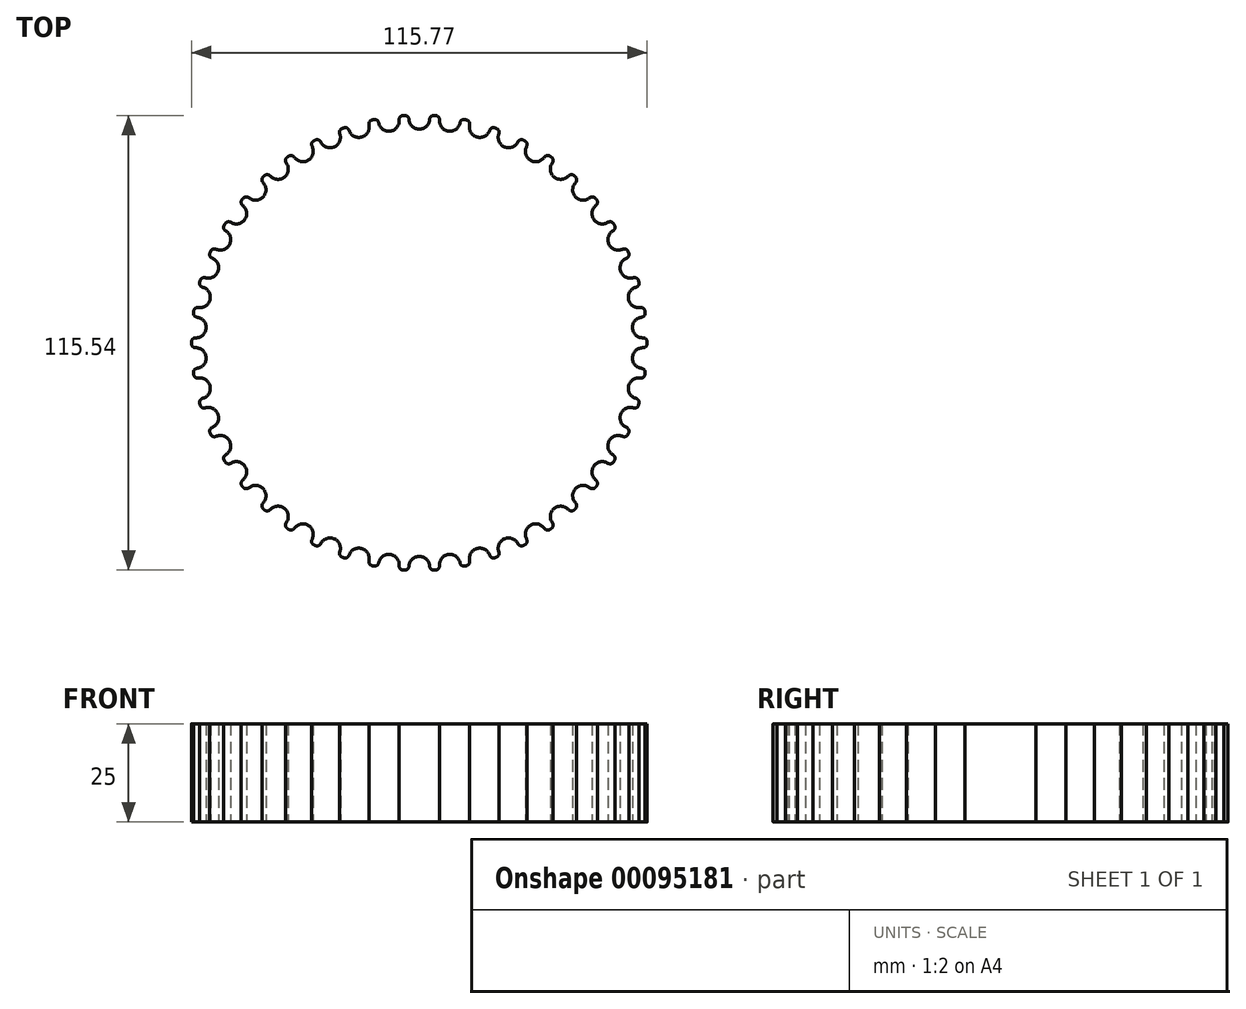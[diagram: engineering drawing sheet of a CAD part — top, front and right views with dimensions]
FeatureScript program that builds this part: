
annotation { "Feature Type Name" : "Feature", "Feature Type Description" : "" }
export const myFeature = defineFeature(function(context is Context, id is Id, definition is map)
    precondition{}
    {
        {
            var Q0;
            Q0=qCreatedBy(makeId("Top.planeOp"),FACE);
            var sketch = newSketch(context, id + "F0", { "sketchPlane" : qUnion([Q0])});
            skArc(sketch, "E0", {"start": v(-3.73, 57.76) * mm, "mid": v(-3.95, 57.75) * mm, "end": v(-4.17, 57.73) * mm});
            skCircle(sketch, "E1", {"center": v(0, 0) * mm, "radius": 54.28 * mm, "construction": true});
            skLineSegment(sketch, "E2", {"start": v(0, 0) * mm, "end": v(0, 57.88) * mm, "construction": true});
            skArc(sketch, "E3", {"start": v(-2.6, 56.59) * mm, "mid": v(0, 54.28) * mm, "end": v(2.6, 56.59) * mm});
            skArc(sketch, "E4", {"start": v(-2.64, 56.87) * mm, "mid": v(-3, 57.53) * mm, "end": v(-3.73, 57.76) * mm});
            skArc(sketch, "E5", {"start": v(3.73, 57.76) * mm, "mid": v(3, 57.53) * mm, "end": v(2.64, 56.87) * mm});
            skLineSegment(sketch, "E6", {"start": v(-2.64, 56.87) * mm, "end": v(-2.6, 56.59) * mm});
            skLineSegment(sketch, "E7", {"start": v(2.6, 56.59) * mm, "end": v(2.64, 56.87) * mm});
            skArc(sketch, "E8.1.0", {"start": v(-10.36, 55.98) * mm, "mid": v(-10.81, 56.59) * mm, "end": v(-11.56, 56.72) * mm});
            skLineSegment(sketch, "E8.1.1", {"start": v(-10.36, 55.98) * mm, "end": v(-10.3, 55.7) * mm});
            skArc(sketch, "E8.1.2", {"start": v(-10.3, 55.7) * mm, "mid": v(-7.4, 53.78) * mm, "end": v(-5.12, 56.42) * mm});
            skLineSegment(sketch, "E8.1.3", {"start": v(-5.12, 56.42) * mm, "end": v(-5.12, 56.7) * mm});
            skArc(sketch, "E8.1.4", {"start": v(-4.17, 57.73) * mm, "mid": v(-4.86, 57.4) * mm, "end": v(-5.12, 56.7) * mm});
            skArc(sketch, "E8.2.0", {"start": v(-17.89, 54.05) * mm, "mid": v(-18.42, 54.59) * mm, "end": v(-19.17, 54.62) * mm});
            skLineSegment(sketch, "E8.2.1", {"start": v(-17.89, 54.05) * mm, "end": v(-17.78, 53.79) * mm});
            skArc(sketch, "E8.2.2", {"start": v(-17.78, 53.79) * mm, "mid": v(-14.64, 52.27) * mm, "end": v(-12.76, 55.2) * mm});
            skLineSegment(sketch, "E8.2.3", {"start": v(-12.76, 55.2) * mm, "end": v(-12.8, 55.47) * mm});
            skArc(sketch, "E8.2.4", {"start": v(-12, 56.63) * mm, "mid": v(-12.63, 56.2) * mm, "end": v(-12.8, 55.47) * mm});
            skArc(sketch, "E8.3.0", {"start": v(-25.08, 51.1) * mm, "mid": v(-25.68, 51.57) * mm, "end": v(-26.43, 51.5) * mm});
            skLineSegment(sketch, "E8.3.1", {"start": v(-25.08, 51.1) * mm, "end": v(-24.94, 50.87) * mm});
            skArc(sketch, "E8.3.2", {"start": v(-24.94, 50.87) * mm, "mid": v(-21.63, 49.79) * mm, "end": v(-20.15, 52.94) * mm});
            skLineSegment(sketch, "E8.3.3", {"start": v(-20.15, 52.94) * mm, "end": v(-20.23, 53.21) * mm});
            skArc(sketch, "E8.3.4", {"start": v(-19.6, 54.47) * mm, "mid": v(-20.16, 53.97) * mm, "end": v(-20.23, 53.21) * mm});
            skArc(sketch, "E8.4.0", {"start": v(-31.8, 47.22) * mm, "mid": v(-32.46, 47.6) * mm, "end": v(-33.2, 47.42) * mm});
            skLineSegment(sketch, "E8.4.1", {"start": v(-31.8, 47.22) * mm, "end": v(-31.63, 47) * mm});
            skArc(sketch, "E8.4.2", {"start": v(-31.63, 47) * mm, "mid": v(-28.2, 46.38) * mm, "end": v(-27.17, 49.7) * mm});
            skLineSegment(sketch, "E8.4.3", {"start": v(-27.17, 49.7) * mm, "end": v(-27.29, 49.96) * mm});
            skArc(sketch, "E8.4.4", {"start": v(-26.83, 51.3) * mm, "mid": v(-27.32, 50.72) * mm, "end": v(-27.29, 49.96) * mm});
            skArc(sketch, "E8.5.0", {"start": v(-37.94, 42.44) * mm, "mid": v(-38.64, 42.73) * mm, "end": v(-39.34, 42.46) * mm});
            skLineSegment(sketch, "E8.5.1", {"start": v(-37.94, 42.44) * mm, "end": v(-37.74, 42.25) * mm});
            skArc(sketch, "E8.5.2", {"start": v(-37.74, 42.25) * mm, "mid": v(-34.26, 42.1) * mm, "end": v(-33.69, 45.54) * mm});
            skLineSegment(sketch, "E8.5.3", {"start": v(-33.69, 45.54) * mm, "end": v(-33.84, 45.78) * mm});
            skArc(sketch, "E8.5.4", {"start": v(-33.56, 47.16) * mm, "mid": v(-33.98, 46.53) * mm, "end": v(-33.84, 45.78) * mm});
            skArc(sketch, "E8.6.0", {"start": v(-43.37, 36.88) * mm, "mid": v(-44.1, 37.07) * mm, "end": v(-44.76, 36.7) * mm});
            skLineSegment(sketch, "E8.6.1", {"start": v(-43.37, 36.88) * mm, "end": v(-43.14, 36.72) * mm});
            skArc(sketch, "E8.6.2", {"start": v(-43.14, 36.72) * mm, "mid": v(-39.67, 37.05) * mm, "end": v(-39.58, 40.53) * mm});
            skLineSegment(sketch, "E8.6.3", {"start": v(-39.58, 40.53) * mm, "end": v(-39.76, 40.75) * mm});
            skArc(sketch, "E8.6.4", {"start": v(-39.67, 42.15) * mm, "mid": v(-40, 41.47) * mm, "end": v(-39.76, 40.75) * mm});
            skArc(sketch, "E8.7.0", {"start": v(-47.98, 30.63) * mm, "mid": v(-48.74, 30.72) * mm, "end": v(-49.34, 30.27) * mm});
            skLineSegment(sketch, "E8.7.1", {"start": v(-47.98, 30.63) * mm, "end": v(-47.74, 30.5) * mm});
            skArc(sketch, "E8.7.2", {"start": v(-47.74, 30.5) * mm, "mid": v(-44.35, 31.3) * mm, "end": v(-44.73, 34.77) * mm});
            skLineSegment(sketch, "E8.7.3", {"start": v(-44.73, 34.77) * mm, "end": v(-44.93, 34.95) * mm});
            skArc(sketch, "E8.7.4", {"start": v(-45.04, 36.36) * mm, "mid": v(-45.27, 35.63) * mm, "end": v(-44.93, 34.95) * mm});
            skArc(sketch, "E8.8.0", {"start": v(-51.7, 23.82) * mm, "mid": v(-52.46, 23.8) * mm, "end": v(-53, 23.27) * mm});
            skLineSegment(sketch, "E8.8.1", {"start": v(-51.7, 23.82) * mm, "end": v(-51.45, 23.72) * mm});
            skArc(sketch, "E8.8.2", {"start": v(-51.45, 23.72) * mm, "mid": v(-48.2, 24.97) * mm, "end": v(-49.04, 28.35) * mm});
            skLineSegment(sketch, "E8.8.3", {"start": v(-49.04, 28.35) * mm, "end": v(-49.28, 28.51) * mm});
            skArc(sketch, "E8.8.4", {"start": v(-49.57, 29.88) * mm, "mid": v(-49.7, 29.14) * mm, "end": v(-49.28, 28.51) * mm});
            skArc(sketch, "E8.9.0", {"start": v(-54.47, 16.55) * mm, "mid": v(-55.22, 16.43) * mm, "end": v(-55.68, 15.83) * mm});
            skLineSegment(sketch, "E8.9.1", {"start": v(-54.47, 16.55) * mm, "end": v(-54.2, 16.5) * mm});
            skArc(sketch, "E8.9.2", {"start": v(-54.2, 16.5) * mm, "mid": v(-51.15, 18.18) * mm, "end": v(-52.45, 21.4) * mm});
            skLineSegment(sketch, "E8.9.3", {"start": v(-52.45, 21.4) * mm, "end": v(-52.7, 21.53) * mm});
            skArc(sketch, "E8.9.4", {"start": v(-53.18, 22.86) * mm, "mid": v(-53.2, 22.1) * mm, "end": v(-52.7, 21.53) * mm});
            skArc(sketch, "E8.10.0", {"start": v(-56.22, 8.98) * mm, "mid": v(-56.94, 8.76) * mm, "end": v(-57.31, 8.1) * mm});
            skLineSegment(sketch, "E8.10.1", {"start": v(-56.22, 8.98) * mm, "end": v(-55.94, 8.96) * mm});
            skArc(sketch, "E8.10.2", {"start": v(-55.94, 8.96) * mm, "mid": v(-53.15, 11.04) * mm, "end": v(-54.88, 14.07) * mm});
            skLineSegment(sketch, "E8.10.3", {"start": v(-54.88, 14.07) * mm, "end": v(-55.14, 14.16) * mm});
            skArc(sketch, "E8.10.4", {"start": v(-55.8, 15.4) * mm, "mid": v(-55.72, 14.65) * mm, "end": v(-55.14, 14.16) * mm});
            skArc(sketch, "E8.11.0", {"start": v(-56.92, 1.24) * mm, "mid": v(-57.6, 0.93) * mm, "end": v(-57.88, 0.22) * mm});
            skLineSegment(sketch, "E8.11.1", {"start": v(-56.92, 1.24) * mm, "end": v(-56.64, 1.26) * mm});
            skArc(sketch, "E8.11.2", {"start": v(-56.64, 1.26) * mm, "mid": v(-54.15, 3.7) * mm, "end": v(-56.28, 6.47) * mm});
            skLineSegment(sketch, "E8.11.3", {"start": v(-56.28, 6.47) * mm, "end": v(-56.55, 6.52) * mm});
            skArc(sketch, "E8.11.4", {"start": v(-57.38, 7.66) * mm, "mid": v(-57.2, 6.93) * mm, "end": v(-56.55, 6.52) * mm});
            skArc(sketch, "E8.12.0", {"start": v(-56.55, -6.52) * mm, "mid": v(-57.2, -6.93) * mm, "end": v(-57.38, -7.66) * mm});
            skLineSegment(sketch, "E8.12.1", {"start": v(-56.55, -6.52) * mm, "end": v(-56.28, -6.47) * mm});
            skArc(sketch, "E8.12.2", {"start": v(-56.28, -6.47) * mm, "mid": v(-54.15, -3.7) * mm, "end": v(-56.64, -1.26) * mm});
            skLineSegment(sketch, "E8.12.3", {"start": v(-56.64, -1.26) * mm, "end": v(-56.92, -1.24) * mm});
            skArc(sketch, "E8.12.4", {"start": v(-57.88, -0.22) * mm, "mid": v(-57.6, -0.93) * mm, "end": v(-56.92, -1.24) * mm});
            skArc(sketch, "E8.13.0", {"start": v(-55.14, -14.16) * mm, "mid": v(-55.72, -14.65) * mm, "end": v(-55.8, -15.4) * mm});
            skLineSegment(sketch, "E8.13.1", {"start": v(-55.14, -14.16) * mm, "end": v(-54.88, -14.07) * mm});
            skArc(sketch, "E8.13.2", {"start": v(-54.88, -14.07) * mm, "mid": v(-53.15, -11.04) * mm, "end": v(-55.94, -8.96) * mm});
            skLineSegment(sketch, "E8.13.3", {"start": v(-55.94, -8.96) * mm, "end": v(-56.22, -8.98) * mm});
            skArc(sketch, "E8.13.4", {"start": v(-57.31, -8.1) * mm, "mid": v(-56.94, -8.76) * mm, "end": v(-56.22, -8.98) * mm});
            skArc(sketch, "E8.14.0", {"start": v(-52.7, -21.53) * mm, "mid": v(-53.2, -22.1) * mm, "end": v(-53.18, -22.86) * mm});
            skLineSegment(sketch, "E8.14.1", {"start": v(-52.7, -21.53) * mm, "end": v(-52.45, -21.4) * mm});
            skArc(sketch, "E8.14.2", {"start": v(-52.45, -21.4) * mm, "mid": v(-51.15, -18.18) * mm, "end": v(-54.2, -16.5) * mm});
            skLineSegment(sketch, "E8.14.3", {"start": v(-54.2, -16.5) * mm, "end": v(-54.47, -16.55) * mm});
            skArc(sketch, "E8.14.4", {"start": v(-55.68, -15.83) * mm, "mid": v(-55.22, -16.43) * mm, "end": v(-54.47, -16.55) * mm});
            skArc(sketch, "E8.15.0", {"start": v(-49.28, -28.51) * mm, "mid": v(-49.7, -29.14) * mm, "end": v(-49.57, -29.88) * mm});
            skLineSegment(sketch, "E8.15.1", {"start": v(-49.28, -28.51) * mm, "end": v(-49.04, -28.35) * mm});
            skArc(sketch, "E8.15.2", {"start": v(-49.04, -28.35) * mm, "mid": v(-48.2, -24.97) * mm, "end": v(-51.45, -23.72) * mm});
            skLineSegment(sketch, "E8.15.3", {"start": v(-51.45, -23.72) * mm, "end": v(-51.7, -23.82) * mm});
            skArc(sketch, "E8.15.4", {"start": v(-53, -23.27) * mm, "mid": v(-52.46, -23.8) * mm, "end": v(-51.7, -23.82) * mm});
            skArc(sketch, "E8.16.0", {"start": v(-44.93, -34.95) * mm, "mid": v(-45.27, -35.63) * mm, "end": v(-45.04, -36.36) * mm});
            skLineSegment(sketch, "E8.16.1", {"start": v(-44.93, -34.95) * mm, "end": v(-44.73, -34.77) * mm});
            skArc(sketch, "E8.16.2", {"start": v(-44.73, -34.77) * mm, "mid": v(-44.35, -31.3) * mm, "end": v(-47.74, -30.5) * mm});
            skLineSegment(sketch, "E8.16.3", {"start": v(-47.74, -30.5) * mm, "end": v(-47.98, -30.63) * mm});
            skArc(sketch, "E8.16.4", {"start": v(-49.34, -30.27) * mm, "mid": v(-48.74, -30.72) * mm, "end": v(-47.98, -30.63) * mm});
            skArc(sketch, "E8.17.0", {"start": v(-39.76, -40.75) * mm, "mid": v(-40, -41.47) * mm, "end": v(-39.67, -42.15) * mm});
            skLineSegment(sketch, "E8.17.1", {"start": v(-39.76, -40.75) * mm, "end": v(-39.58, -40.53) * mm});
            skArc(sketch, "E8.17.2", {"start": v(-39.58, -40.53) * mm, "mid": v(-39.67, -37.05) * mm, "end": v(-43.14, -36.72) * mm});
            skLineSegment(sketch, "E8.17.3", {"start": v(-43.14, -36.72) * mm, "end": v(-43.37, -36.88) * mm});
            skArc(sketch, "E8.17.4", {"start": v(-44.76, -36.7) * mm, "mid": v(-44.1, -37.07) * mm, "end": v(-43.37, -36.88) * mm});
            skArc(sketch, "E8.18.0", {"start": v(-33.84, -45.78) * mm, "mid": v(-33.98, -46.53) * mm, "end": v(-33.56, -47.16) * mm});
            skLineSegment(sketch, "E8.18.1", {"start": v(-33.84, -45.78) * mm, "end": v(-33.69, -45.54) * mm});
            skArc(sketch, "E8.18.2", {"start": v(-33.69, -45.54) * mm, "mid": v(-34.26, -42.1) * mm, "end": v(-37.74, -42.25) * mm});
            skLineSegment(sketch, "E8.18.3", {"start": v(-37.74, -42.25) * mm, "end": v(-37.94, -42.44) * mm});
            skArc(sketch, "E8.18.4", {"start": v(-39.34, -42.46) * mm, "mid": v(-38.64, -42.73) * mm, "end": v(-37.94, -42.44) * mm});
            skArc(sketch, "E8.19.0", {"start": v(-27.29, -49.96) * mm, "mid": v(-27.32, -50.72) * mm, "end": v(-26.83, -51.3) * mm});
            skLineSegment(sketch, "E8.19.1", {"start": v(-27.29, -49.96) * mm, "end": v(-27.17, -49.7) * mm});
            skArc(sketch, "E8.19.2", {"start": v(-27.17, -49.7) * mm, "mid": v(-28.2, -46.38) * mm, "end": v(-31.63, -47) * mm});
            skLineSegment(sketch, "E8.19.3", {"start": v(-31.63, -47) * mm, "end": v(-31.8, -47.22) * mm});
            skArc(sketch, "E8.19.4", {"start": v(-33.2, -47.42) * mm, "mid": v(-32.46, -47.6) * mm, "end": v(-31.8, -47.22) * mm});
            skArc(sketch, "E8.20.0", {"start": v(-20.23, -53.21) * mm, "mid": v(-20.16, -53.97) * mm, "end": v(-19.6, -54.47) * mm});
            skLineSegment(sketch, "E8.20.1", {"start": v(-20.23, -53.21) * mm, "end": v(-20.15, -52.94) * mm});
            skArc(sketch, "E8.20.2", {"start": v(-20.15, -52.94) * mm, "mid": v(-21.63, -49.79) * mm, "end": v(-24.94, -50.87) * mm});
            skLineSegment(sketch, "E8.20.3", {"start": v(-24.94, -50.87) * mm, "end": v(-25.08, -51.1) * mm});
            skArc(sketch, "E8.20.4", {"start": v(-26.43, -51.5) * mm, "mid": v(-25.68, -51.57) * mm, "end": v(-25.08, -51.1) * mm});
            skArc(sketch, "E8.21.0", {"start": v(-12.8, -55.47) * mm, "mid": v(-12.63, -56.2) * mm, "end": v(-12, -56.63) * mm});
            skLineSegment(sketch, "E8.21.1", {"start": v(-12.8, -55.47) * mm, "end": v(-12.76, -55.2) * mm});
            skArc(sketch, "E8.21.2", {"start": v(-12.76, -55.2) * mm, "mid": v(-14.64, -52.27) * mm, "end": v(-17.78, -53.79) * mm});
            skLineSegment(sketch, "E8.21.3", {"start": v(-17.78, -53.79) * mm, "end": v(-17.89, -54.05) * mm});
            skArc(sketch, "E8.21.4", {"start": v(-19.17, -54.62) * mm, "mid": v(-18.42, -54.59) * mm, "end": v(-17.89, -54.05) * mm});
            skArc(sketch, "E8.22.0", {"start": v(-5.12, -56.7) * mm, "mid": v(-4.86, -57.4) * mm, "end": v(-4.17, -57.73) * mm});
            skLineSegment(sketch, "E8.22.1", {"start": v(-5.12, -56.7) * mm, "end": v(-5.12, -56.42) * mm});
            skArc(sketch, "E8.22.2", {"start": v(-5.12, -56.42) * mm, "mid": v(-7.4, -53.78) * mm, "end": v(-10.3, -55.7) * mm});
            skLineSegment(sketch, "E8.22.3", {"start": v(-10.3, -55.7) * mm, "end": v(-10.36, -55.98) * mm});
            skArc(sketch, "E8.22.4", {"start": v(-11.56, -56.72) * mm, "mid": v(-10.81, -56.59) * mm, "end": v(-10.36, -55.98) * mm});
            skArc(sketch, "E8.23.0", {"start": v(2.64, -56.87) * mm, "mid": v(3, -57.53) * mm, "end": v(3.73, -57.76) * mm});
            skLineSegment(sketch, "E8.23.1", {"start": v(2.64, -56.87) * mm, "end": v(2.6, -56.59) * mm});
            skArc(sketch, "E8.23.2", {"start": v(2.6, -56.59) * mm, "mid": v(0, -54.28) * mm, "end": v(-2.6, -56.59) * mm});
            skLineSegment(sketch, "E8.23.3", {"start": v(-2.6, -56.59) * mm, "end": v(-2.64, -56.87) * mm});
            skArc(sketch, "E8.23.4", {"start": v(-3.73, -57.76) * mm, "mid": v(-3, -57.53) * mm, "end": v(-2.64, -56.87) * mm});
            skArc(sketch, "E8.24.0", {"start": v(10.36, -55.98) * mm, "mid": v(10.81, -56.59) * mm, "end": v(11.56, -56.72) * mm});
            skLineSegment(sketch, "E8.24.1", {"start": v(10.36, -55.98) * mm, "end": v(10.3, -55.7) * mm});
            skArc(sketch, "E8.24.2", {"start": v(10.3, -55.7) * mm, "mid": v(7.4, -53.78) * mm, "end": v(5.12, -56.42) * mm});
            skLineSegment(sketch, "E8.24.3", {"start": v(5.12, -56.42) * mm, "end": v(5.12, -56.7) * mm});
            skArc(sketch, "E8.24.4", {"start": v(4.17, -57.73) * mm, "mid": v(4.86, -57.4) * mm, "end": v(5.12, -56.7) * mm});
            skArc(sketch, "E8.25.0", {"start": v(17.89, -54.05) * mm, "mid": v(18.42, -54.59) * mm, "end": v(19.17, -54.62) * mm});
            skLineSegment(sketch, "E8.25.1", {"start": v(17.89, -54.05) * mm, "end": v(17.78, -53.79) * mm});
            skArc(sketch, "E8.25.2", {"start": v(17.78, -53.79) * mm, "mid": v(14.64, -52.27) * mm, "end": v(12.76, -55.2) * mm});
            skLineSegment(sketch, "E8.25.3", {"start": v(12.76, -55.2) * mm, "end": v(12.8, -55.47) * mm});
            skArc(sketch, "E8.25.4", {"start": v(12, -56.63) * mm, "mid": v(12.63, -56.2) * mm, "end": v(12.8, -55.47) * mm});
            skArc(sketch, "E8.26.0", {"start": v(25.08, -51.1) * mm, "mid": v(25.68, -51.57) * mm, "end": v(26.43, -51.5) * mm});
            skLineSegment(sketch, "E8.26.1", {"start": v(25.08, -51.1) * mm, "end": v(24.94, -50.87) * mm});
            skArc(sketch, "E8.26.2", {"start": v(24.94, -50.87) * mm, "mid": v(21.63, -49.79) * mm, "end": v(20.15, -52.94) * mm});
            skLineSegment(sketch, "E8.26.3", {"start": v(20.15, -52.94) * mm, "end": v(20.23, -53.21) * mm});
            skArc(sketch, "E8.26.4", {"start": v(19.6, -54.47) * mm, "mid": v(20.16, -53.97) * mm, "end": v(20.23, -53.21) * mm});
            skArc(sketch, "E8.27.0", {"start": v(31.8, -47.22) * mm, "mid": v(32.46, -47.6) * mm, "end": v(33.2, -47.42) * mm});
            skLineSegment(sketch, "E8.27.1", {"start": v(31.8, -47.22) * mm, "end": v(31.63, -47) * mm});
            skArc(sketch, "E8.27.2", {"start": v(31.63, -47) * mm, "mid": v(28.2, -46.38) * mm, "end": v(27.17, -49.7) * mm});
            skLineSegment(sketch, "E8.27.3", {"start": v(27.17, -49.7) * mm, "end": v(27.29, -49.96) * mm});
            skArc(sketch, "E8.27.4", {"start": v(26.83, -51.3) * mm, "mid": v(27.32, -50.72) * mm, "end": v(27.29, -49.96) * mm});
            skArc(sketch, "E8.28.0", {"start": v(37.94, -42.44) * mm, "mid": v(38.64, -42.73) * mm, "end": v(39.34, -42.46) * mm});
            skLineSegment(sketch, "E8.28.1", {"start": v(37.94, -42.44) * mm, "end": v(37.74, -42.25) * mm});
            skArc(sketch, "E8.28.2", {"start": v(37.74, -42.25) * mm, "mid": v(34.26, -42.1) * mm, "end": v(33.69, -45.54) * mm});
            skLineSegment(sketch, "E8.28.3", {"start": v(33.69, -45.54) * mm, "end": v(33.84, -45.78) * mm});
            skArc(sketch, "E8.28.4", {"start": v(33.56, -47.16) * mm, "mid": v(33.98, -46.53) * mm, "end": v(33.84, -45.78) * mm});
            skArc(sketch, "E8.29.0", {"start": v(43.37, -36.88) * mm, "mid": v(44.1, -37.07) * mm, "end": v(44.76, -36.7) * mm});
            skLineSegment(sketch, "E8.29.1", {"start": v(43.37, -36.88) * mm, "end": v(43.14, -36.72) * mm});
            skArc(sketch, "E8.29.2", {"start": v(43.14, -36.72) * mm, "mid": v(39.67, -37.05) * mm, "end": v(39.58, -40.53) * mm});
            skLineSegment(sketch, "E8.29.3", {"start": v(39.58, -40.53) * mm, "end": v(39.76, -40.75) * mm});
            skArc(sketch, "E8.29.4", {"start": v(39.67, -42.15) * mm, "mid": v(40, -41.47) * mm, "end": v(39.76, -40.75) * mm});
            skArc(sketch, "E8.30.0", {"start": v(47.98, -30.63) * mm, "mid": v(48.74, -30.72) * mm, "end": v(49.34, -30.27) * mm});
            skLineSegment(sketch, "E8.30.1", {"start": v(47.98, -30.63) * mm, "end": v(47.74, -30.5) * mm});
            skArc(sketch, "E8.30.2", {"start": v(47.74, -30.5) * mm, "mid": v(44.35, -31.3) * mm, "end": v(44.73, -34.77) * mm});
            skLineSegment(sketch, "E8.30.3", {"start": v(44.73, -34.77) * mm, "end": v(44.93, -34.95) * mm});
            skArc(sketch, "E8.30.4", {"start": v(45.04, -36.36) * mm, "mid": v(45.27, -35.63) * mm, "end": v(44.93, -34.95) * mm});
            skArc(sketch, "E8.31.0", {"start": v(51.7, -23.82) * mm, "mid": v(52.46, -23.8) * mm, "end": v(53, -23.27) * mm});
            skLineSegment(sketch, "E8.31.1", {"start": v(51.7, -23.82) * mm, "end": v(51.45, -23.72) * mm});
            skArc(sketch, "E8.31.2", {"start": v(51.45, -23.72) * mm, "mid": v(48.2, -24.97) * mm, "end": v(49.04, -28.35) * mm});
            skLineSegment(sketch, "E8.31.3", {"start": v(49.04, -28.35) * mm, "end": v(49.28, -28.51) * mm});
            skArc(sketch, "E8.31.4", {"start": v(49.57, -29.88) * mm, "mid": v(49.7, -29.14) * mm, "end": v(49.28, -28.51) * mm});
            skArc(sketch, "E8.32.0", {"start": v(54.47, -16.55) * mm, "mid": v(55.22, -16.43) * mm, "end": v(55.68, -15.83) * mm});
            skLineSegment(sketch, "E8.32.1", {"start": v(54.47, -16.55) * mm, "end": v(54.2, -16.5) * mm});
            skArc(sketch, "E8.32.2", {"start": v(54.2, -16.5) * mm, "mid": v(51.15, -18.18) * mm, "end": v(52.45, -21.4) * mm});
            skLineSegment(sketch, "E8.32.3", {"start": v(52.45, -21.4) * mm, "end": v(52.7, -21.53) * mm});
            skArc(sketch, "E8.32.4", {"start": v(53.18, -22.86) * mm, "mid": v(53.2, -22.1) * mm, "end": v(52.7, -21.53) * mm});
            skArc(sketch, "E8.33.0", {"start": v(56.22, -8.98) * mm, "mid": v(56.94, -8.76) * mm, "end": v(57.31, -8.1) * mm});
            skLineSegment(sketch, "E8.33.1", {"start": v(56.22, -8.98) * mm, "end": v(55.94, -8.96) * mm});
            skArc(sketch, "E8.33.2", {"start": v(55.94, -8.96) * mm, "mid": v(53.15, -11.04) * mm, "end": v(54.88, -14.07) * mm});
            skLineSegment(sketch, "E8.33.3", {"start": v(54.88, -14.07) * mm, "end": v(55.14, -14.16) * mm});
            skArc(sketch, "E8.33.4", {"start": v(55.8, -15.4) * mm, "mid": v(55.72, -14.65) * mm, "end": v(55.14, -14.16) * mm});
            skArc(sketch, "E8.34.0", {"start": v(56.92, -1.24) * mm, "mid": v(57.6, -0.93) * mm, "end": v(57.88, -0.22) * mm});
            skLineSegment(sketch, "E8.34.1", {"start": v(56.92, -1.24) * mm, "end": v(56.64, -1.26) * mm});
            skArc(sketch, "E8.34.2", {"start": v(56.64, -1.26) * mm, "mid": v(54.15, -3.7) * mm, "end": v(56.28, -6.47) * mm});
            skLineSegment(sketch, "E8.34.3", {"start": v(56.28, -6.47) * mm, "end": v(56.55, -6.52) * mm});
            skArc(sketch, "E8.34.4", {"start": v(57.38, -7.66) * mm, "mid": v(57.2, -6.93) * mm, "end": v(56.55, -6.52) * mm});
            skArc(sketch, "E8.35.0", {"start": v(56.55, 6.52) * mm, "mid": v(57.2, 6.93) * mm, "end": v(57.38, 7.66) * mm});
            skLineSegment(sketch, "E8.35.1", {"start": v(56.55, 6.52) * mm, "end": v(56.28, 6.47) * mm});
            skArc(sketch, "E8.35.2", {"start": v(56.28, 6.47) * mm, "mid": v(54.15, 3.7) * mm, "end": v(56.64, 1.26) * mm});
            skLineSegment(sketch, "E8.35.3", {"start": v(56.64, 1.26) * mm, "end": v(56.92, 1.24) * mm});
            skArc(sketch, "E8.35.4", {"start": v(57.88, 0.22) * mm, "mid": v(57.6, 0.93) * mm, "end": v(56.92, 1.24) * mm});
            skArc(sketch, "E8.36.0", {"start": v(55.14, 14.16) * mm, "mid": v(55.72, 14.65) * mm, "end": v(55.8, 15.4) * mm});
            skLineSegment(sketch, "E8.36.1", {"start": v(55.14, 14.16) * mm, "end": v(54.88, 14.07) * mm});
            skArc(sketch, "E8.36.2", {"start": v(54.88, 14.07) * mm, "mid": v(53.15, 11.04) * mm, "end": v(55.94, 8.96) * mm});
            skLineSegment(sketch, "E8.36.3", {"start": v(55.94, 8.96) * mm, "end": v(56.22, 8.98) * mm});
            skArc(sketch, "E8.36.4", {"start": v(57.31, 8.1) * mm, "mid": v(56.94, 8.76) * mm, "end": v(56.22, 8.98) * mm});
            skArc(sketch, "E8.37.0", {"start": v(52.7, 21.53) * mm, "mid": v(53.2, 22.1) * mm, "end": v(53.18, 22.86) * mm});
            skLineSegment(sketch, "E8.37.1", {"start": v(52.7, 21.53) * mm, "end": v(52.45, 21.4) * mm});
            skArc(sketch, "E8.37.2", {"start": v(52.45, 21.4) * mm, "mid": v(51.15, 18.18) * mm, "end": v(54.2, 16.5) * mm});
            skLineSegment(sketch, "E8.37.3", {"start": v(54.2, 16.5) * mm, "end": v(54.47, 16.55) * mm});
            skArc(sketch, "E8.37.4", {"start": v(55.68, 15.83) * mm, "mid": v(55.22, 16.43) * mm, "end": v(54.47, 16.55) * mm});
            skArc(sketch, "E8.38.0", {"start": v(49.28, 28.51) * mm, "mid": v(49.7, 29.14) * mm, "end": v(49.57, 29.88) * mm});
            skLineSegment(sketch, "E8.38.1", {"start": v(49.28, 28.51) * mm, "end": v(49.04, 28.35) * mm});
            skArc(sketch, "E8.38.2", {"start": v(49.04, 28.35) * mm, "mid": v(48.2, 24.97) * mm, "end": v(51.45, 23.72) * mm});
            skLineSegment(sketch, "E8.38.3", {"start": v(51.45, 23.72) * mm, "end": v(51.7, 23.82) * mm});
            skArc(sketch, "E8.38.4", {"start": v(53, 23.27) * mm, "mid": v(52.46, 23.8) * mm, "end": v(51.7, 23.82) * mm});
            skArc(sketch, "E8.39.0", {"start": v(44.93, 34.95) * mm, "mid": v(45.27, 35.63) * mm, "end": v(45.04, 36.36) * mm});
            skLineSegment(sketch, "E8.39.1", {"start": v(44.93, 34.95) * mm, "end": v(44.73, 34.77) * mm});
            skArc(sketch, "E8.39.2", {"start": v(44.73, 34.77) * mm, "mid": v(44.35, 31.3) * mm, "end": v(47.74, 30.5) * mm});
            skLineSegment(sketch, "E8.39.3", {"start": v(47.74, 30.5) * mm, "end": v(47.98, 30.63) * mm});
            skArc(sketch, "E8.39.4", {"start": v(49.34, 30.27) * mm, "mid": v(48.74, 30.72) * mm, "end": v(47.98, 30.63) * mm});
            skArc(sketch, "E8.40.0", {"start": v(39.76, 40.75) * mm, "mid": v(40, 41.47) * mm, "end": v(39.67, 42.15) * mm});
            skLineSegment(sketch, "E8.40.1", {"start": v(39.76, 40.75) * mm, "end": v(39.58, 40.53) * mm});
            skArc(sketch, "E8.40.2", {"start": v(39.58, 40.53) * mm, "mid": v(39.67, 37.05) * mm, "end": v(43.14, 36.72) * mm});
            skLineSegment(sketch, "E8.40.3", {"start": v(43.14, 36.72) * mm, "end": v(43.37, 36.88) * mm});
            skArc(sketch, "E8.40.4", {"start": v(44.76, 36.7) * mm, "mid": v(44.1, 37.07) * mm, "end": v(43.37, 36.88) * mm});
            skArc(sketch, "E8.41.0", {"start": v(33.84, 45.78) * mm, "mid": v(33.98, 46.53) * mm, "end": v(33.56, 47.16) * mm});
            skLineSegment(sketch, "E8.41.1", {"start": v(33.84, 45.78) * mm, "end": v(33.69, 45.54) * mm});
            skArc(sketch, "E8.41.2", {"start": v(33.69, 45.54) * mm, "mid": v(34.26, 42.1) * mm, "end": v(37.74, 42.25) * mm});
            skLineSegment(sketch, "E8.41.3", {"start": v(37.74, 42.25) * mm, "end": v(37.94, 42.44) * mm});
            skArc(sketch, "E8.41.4", {"start": v(39.34, 42.46) * mm, "mid": v(38.64, 42.73) * mm, "end": v(37.94, 42.44) * mm});
            skArc(sketch, "E8.42.0", {"start": v(27.29, 49.96) * mm, "mid": v(27.32, 50.72) * mm, "end": v(26.83, 51.3) * mm});
            skLineSegment(sketch, "E8.42.1", {"start": v(27.29, 49.96) * mm, "end": v(27.17, 49.7) * mm});
            skArc(sketch, "E8.42.2", {"start": v(27.17, 49.7) * mm, "mid": v(28.2, 46.38) * mm, "end": v(31.63, 47) * mm});
            skLineSegment(sketch, "E8.42.3", {"start": v(31.63, 47) * mm, "end": v(31.8, 47.22) * mm});
            skArc(sketch, "E8.42.4", {"start": v(33.2, 47.42) * mm, "mid": v(32.46, 47.6) * mm, "end": v(31.8, 47.22) * mm});
            skArc(sketch, "E8.43.0", {"start": v(20.23, 53.21) * mm, "mid": v(20.16, 53.97) * mm, "end": v(19.6, 54.47) * mm});
            skLineSegment(sketch, "E8.43.1", {"start": v(20.23, 53.21) * mm, "end": v(20.15, 52.94) * mm});
            skArc(sketch, "E8.43.2", {"start": v(20.15, 52.94) * mm, "mid": v(21.63, 49.79) * mm, "end": v(24.94, 50.87) * mm});
            skLineSegment(sketch, "E8.43.3", {"start": v(24.94, 50.87) * mm, "end": v(25.08, 51.1) * mm});
            skArc(sketch, "E8.43.4", {"start": v(26.43, 51.5) * mm, "mid": v(25.68, 51.57) * mm, "end": v(25.08, 51.1) * mm});
            skArc(sketch, "E8.44.0", {"start": v(12.8, 55.47) * mm, "mid": v(12.63, 56.2) * mm, "end": v(12, 56.63) * mm});
            skLineSegment(sketch, "E8.44.1", {"start": v(12.8, 55.47) * mm, "end": v(12.76, 55.2) * mm});
            skArc(sketch, "E8.44.2", {"start": v(12.76, 55.2) * mm, "mid": v(14.64, 52.27) * mm, "end": v(17.78, 53.79) * mm});
            skLineSegment(sketch, "E8.44.3", {"start": v(17.78, 53.79) * mm, "end": v(17.89, 54.05) * mm});
            skArc(sketch, "E8.44.4", {"start": v(19.17, 54.62) * mm, "mid": v(18.42, 54.59) * mm, "end": v(17.89, 54.05) * mm});
            skArc(sketch, "E8.45.0", {"start": v(5.12, 56.7) * mm, "mid": v(4.86, 57.4) * mm, "end": v(4.17, 57.73) * mm});
            skLineSegment(sketch, "E8.45.1", {"start": v(5.12, 56.7) * mm, "end": v(5.12, 56.42) * mm});
            skArc(sketch, "E8.45.2", {"start": v(5.12, 56.42) * mm, "mid": v(7.4, 53.78) * mm, "end": v(10.3, 55.7) * mm});
            skLineSegment(sketch, "E8.45.3", {"start": v(10.3, 55.7) * mm, "end": v(10.36, 55.98) * mm});
            skArc(sketch, "E8.45.4", {"start": v(11.56, 56.72) * mm, "mid": v(10.81, 56.59) * mm, "end": v(10.36, 55.98) * mm});
            skArc(sketch, "E9.trimOffspring", {"start": v(-11.56, 56.72) * mm, "mid": v(-11.78, 56.67) * mm, "end": v(-12, 56.63) * mm});
            skArc(sketch, "E10.trimOffspring", {"start": v(4.17, 57.73) * mm, "mid": v(3.95, 57.75) * mm, "end": v(3.73, 57.76) * mm});
            skArc(sketch, "E11.trimOffspring", {"start": v(12, 56.63) * mm, "mid": v(11.78, 56.67) * mm, "end": v(11.56, 56.72) * mm});
            skArc(sketch, "E12.trimOffspring", {"start": v(19.6, 54.47) * mm, "mid": v(19.38, 54.54) * mm, "end": v(19.17, 54.62) * mm});
            skArc(sketch, "E13.trimOffspring", {"start": v(26.83, 51.3) * mm, "mid": v(26.63, 51.4) * mm, "end": v(26.43, 51.5) * mm});
            skArc(sketch, "E14.trimOffspring", {"start": v(33.56, 47.16) * mm, "mid": v(33.38, 47.3) * mm, "end": v(33.2, 47.42) * mm});
            skArc(sketch, "E15.trimOffspring", {"start": v(39.67, 42.15) * mm, "mid": v(39.5, 42.3) * mm, "end": v(39.34, 42.46) * mm});
            skArc(sketch, "E16.trimOffspring", {"start": v(45.04, 36.36) * mm, "mid": v(44.9, 36.53) * mm, "end": v(44.76, 36.7) * mm});
            skArc(sketch, "E17.trimOffspring", {"start": v(49.57, 29.88) * mm, "mid": v(49.46, 30.08) * mm, "end": v(49.34, 30.27) * mm});
            skArc(sketch, "E18.trimOffspring", {"start": v(53.18, 22.86) * mm, "mid": v(53.1, 23.06) * mm, "end": v(53, 23.27) * mm});
            skArc(sketch, "E19.trimOffspring", {"start": v(55.8, 15.4) * mm, "mid": v(55.74, 15.62) * mm, "end": v(55.68, 15.83) * mm});
            skArc(sketch, "E20.trimOffspring", {"start": v(57.38, 7.66) * mm, "mid": v(57.35, 7.88) * mm, "end": v(57.31, 8.1) * mm});
            skArc(sketch, "E21.trimOffspring", {"start": v(57.88, -0.22) * mm, "mid": v(57.88, 0) * mm, "end": v(57.88, 0.22) * mm});
            skArc(sketch, "E22.trimOffspring", {"start": v(57.31, -8.1) * mm, "mid": v(57.35, -7.88) * mm, "end": v(57.38, -7.66) * mm});
            skArc(sketch, "E23.trimOffspring", {"start": v(55.68, -15.83) * mm, "mid": v(55.74, -15.62) * mm, "end": v(55.8, -15.4) * mm});
            skArc(sketch, "E24.trimOffspring", {"start": v(53, -23.27) * mm, "mid": v(53.1, -23.06) * mm, "end": v(53.18, -22.86) * mm});
            skArc(sketch, "E25.trimOffspring", {"start": v(49.34, -30.27) * mm, "mid": v(49.46, -30.08) * mm, "end": v(49.57, -29.88) * mm});
            skArc(sketch, "E26.trimOffspring", {"start": v(44.76, -36.7) * mm, "mid": v(44.9, -36.53) * mm, "end": v(45.04, -36.36) * mm});
            skArc(sketch, "E27.trimOffspring", {"start": v(39.34, -42.46) * mm, "mid": v(39.5, -42.3) * mm, "end": v(39.67, -42.15) * mm});
            skArc(sketch, "E28.trimOffspring", {"start": v(19.17, -54.62) * mm, "mid": v(19.38, -54.54) * mm, "end": v(19.6, -54.47) * mm});
            skArc(sketch, "E29.trimOffspring", {"start": v(26.43, -51.5) * mm, "mid": v(26.63, -51.4) * mm, "end": v(26.83, -51.3) * mm});
            skArc(sketch, "E30.trimOffspring", {"start": v(33.2, -47.42) * mm, "mid": v(33.38, -47.3) * mm, "end": v(33.56, -47.16) * mm});
            skArc(sketch, "E31.trimOffspring", {"start": v(11.56, -56.72) * mm, "mid": v(11.78, -56.67) * mm, "end": v(12, -56.63) * mm});
            skArc(sketch, "E32.trimOffspring", {"start": v(3.73, -57.76) * mm, "mid": v(3.95, -57.75) * mm, "end": v(4.17, -57.73) * mm});
            skArc(sketch, "E33.trimOffspring", {"start": v(-4.17, -57.73) * mm, "mid": v(-3.95, -57.75) * mm, "end": v(-3.73, -57.76) * mm});
            skArc(sketch, "E34.trimOffspring", {"start": v(-12, -56.63) * mm, "mid": v(-11.78, -56.67) * mm, "end": v(-11.56, -56.72) * mm});
            skArc(sketch, "E35.trimOffspring", {"start": v(-19.6, -54.47) * mm, "mid": v(-19.38, -54.54) * mm, "end": v(-19.17, -54.62) * mm});
            skArc(sketch, "E36.trimOffspring", {"start": v(-26.83, -51.3) * mm, "mid": v(-26.63, -51.4) * mm, "end": v(-26.43, -51.5) * mm});
            skArc(sketch, "E37.trimOffspring", {"start": v(-33.56, -47.16) * mm, "mid": v(-33.38, -47.3) * mm, "end": v(-33.2, -47.42) * mm});
            skArc(sketch, "E38.trimOffspring", {"start": v(-39.67, -42.15) * mm, "mid": v(-39.5, -42.3) * mm, "end": v(-39.34, -42.46) * mm});
            skArc(sketch, "E39.trimOffspring", {"start": v(-45.04, -36.36) * mm, "mid": v(-44.9, -36.53) * mm, "end": v(-44.76, -36.7) * mm});
            skArc(sketch, "E40.trimOffspring", {"start": v(-49.57, -29.88) * mm, "mid": v(-49.46, -30.08) * mm, "end": v(-49.34, -30.27) * mm});
            skArc(sketch, "E41.trimOffspring", {"start": v(-53.18, -22.86) * mm, "mid": v(-53.1, -23.06) * mm, "end": v(-53, -23.27) * mm});
            skArc(sketch, "E42.trimOffspring", {"start": v(-55.8, -15.4) * mm, "mid": v(-55.74, -15.62) * mm, "end": v(-55.68, -15.83) * mm});
            skArc(sketch, "E43.trimOffspring", {"start": v(-57.38, -7.66) * mm, "mid": v(-57.35, -7.88) * mm, "end": v(-57.31, -8.1) * mm});
            skArc(sketch, "E44.trimOffspring", {"start": v(-57.31, 8.1) * mm, "mid": v(-57.35, 7.88) * mm, "end": v(-57.38, 7.66) * mm});
            skArc(sketch, "E45.trimOffspring", {"start": v(-57.88, 0.22) * mm, "mid": v(-57.88, 0) * mm, "end": v(-57.88, -0.22) * mm});
            skArc(sketch, "E46.trimOffspring", {"start": v(-55.68, 15.83) * mm, "mid": v(-55.74, 15.62) * mm, "end": v(-55.8, 15.4) * mm});
            skArc(sketch, "E47.trimOffspring", {"start": v(-53, 23.27) * mm, "mid": v(-53.1, 23.06) * mm, "end": v(-53.18, 22.86) * mm});
            skArc(sketch, "E48.trimOffspring", {"start": v(-49.34, 30.27) * mm, "mid": v(-49.46, 30.08) * mm, "end": v(-49.57, 29.88) * mm});
            skArc(sketch, "E49.trimOffspring", {"start": v(-44.76, 36.7) * mm, "mid": v(-44.9, 36.53) * mm, "end": v(-45.04, 36.36) * mm});
            skArc(sketch, "E50.trimOffspring", {"start": v(-39.34, 42.46) * mm, "mid": v(-39.5, 42.3) * mm, "end": v(-39.67, 42.15) * mm});
            skArc(sketch, "E51.trimOffspring", {"start": v(-33.2, 47.42) * mm, "mid": v(-33.38, 47.3) * mm, "end": v(-33.56, 47.16) * mm});
            skArc(sketch, "E52.trimOffspring", {"start": v(-26.43, 51.5) * mm, "mid": v(-26.63, 51.4) * mm, "end": v(-26.83, 51.3) * mm});
            skArc(sketch, "E53.trimOffspring", {"start": v(-19.17, 54.62) * mm, "mid": v(-19.38, 54.54) * mm, "end": v(-19.6, 54.47) * mm});
            skSolve(sketch);
        }
        {
            var Q0;
            Q0 = qSketchRegion(id + "F0", true);
            extrude(context, id + "F1", {"entities" : qUnion([Q0]), "depth" : 25 * mm});
        }
    });
